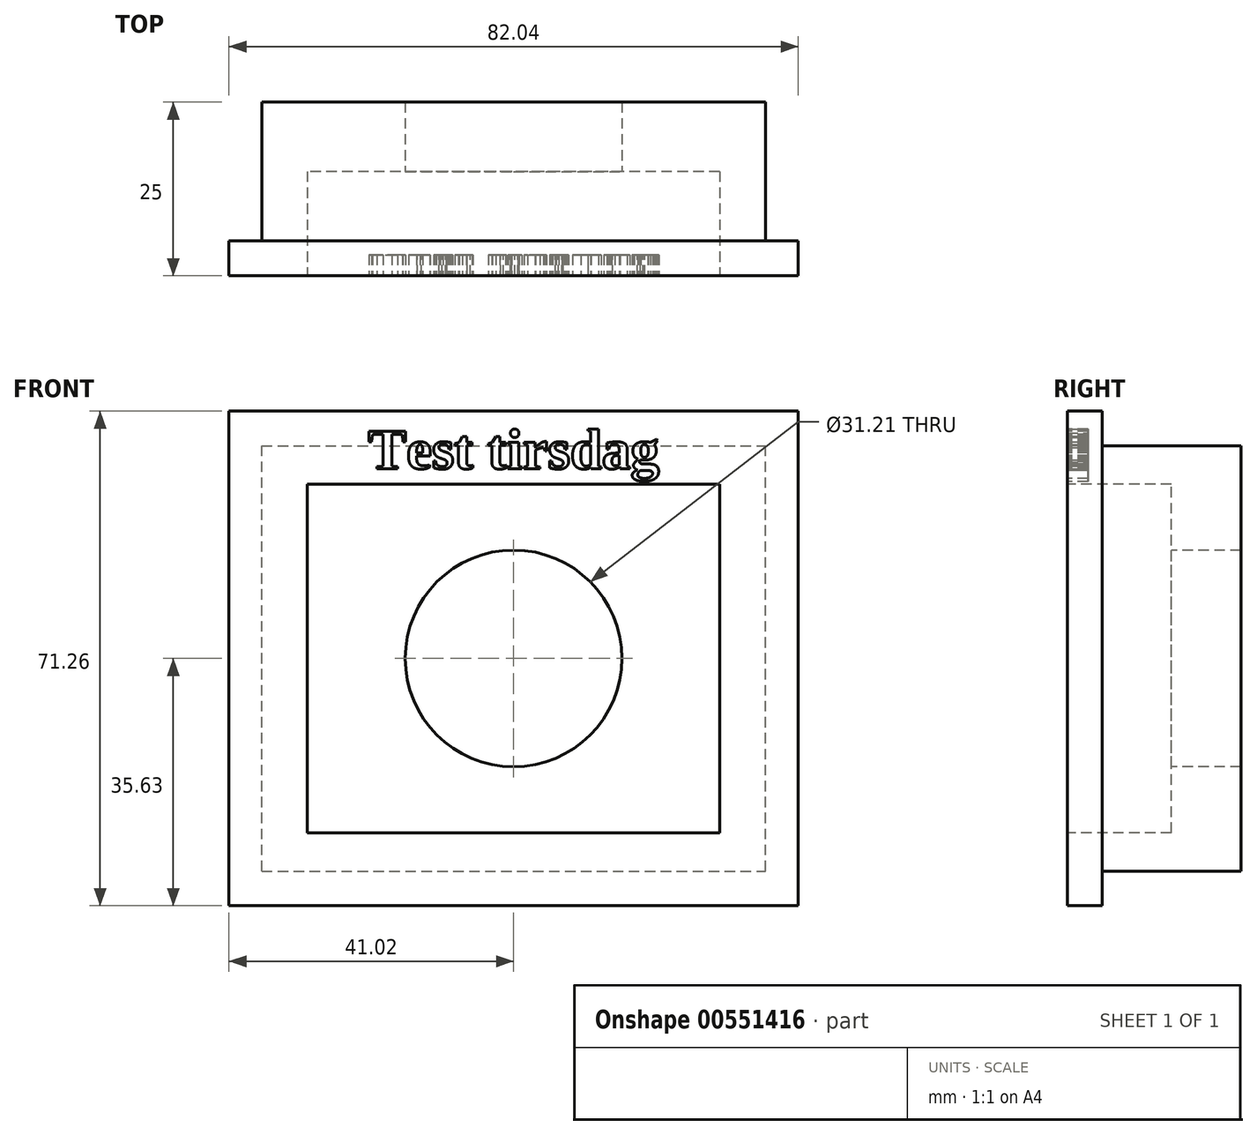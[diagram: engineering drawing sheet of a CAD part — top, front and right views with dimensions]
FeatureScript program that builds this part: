
annotation { "Feature Type Name" : "Feature", "Feature Type Description" : "" }
export const myFeature = defineFeature(function(context is Context, id is Id, definition is map)
    precondition{}
    {
        {
            var Q0;
            Q0=qCreatedBy(makeId("Front.planeOp"),FACE);
            var sketch = newSketch(context, id + "F0", { "sketchPlane" : qUnion([Q0])});
            skLineSegment(sketch, "E0.bottom", {"start": v(41.02, -35.63) * mm, "end": v(-41.02, -35.63) * mm});
            skLineSegment(sketch, "E0.top", {"start": v(41.02, 35.63) * mm, "end": v(-41.02, 35.63) * mm});
            skLineSegment(sketch, "E0.left", {"start": v(41.02, -35.63) * mm, "end": v(41.02, 35.63) * mm});
            skLineSegment(sketch, "E0.right", {"start": v(-41.02, -35.63) * mm, "end": v(-41.02, 35.63) * mm});
            skPoint(sketch, "E0.middle", {"position": v(0, 0) * mm});
            skSolve(sketch);
        }
        {
            var Q0;
            Q0=makeQuery(id+"F0.imprint","IMPRINT",FACE,{"disambiguationData":[TD([[makeQuery(id+"F0.imprint","IMPRINT",EDGE,{"derivedFrom":sQuery(id+"F0.wireOp",EDGE,"E0.bottom")}),-1.0]])]});
            extrude(context, id + "F1", {"entities" : qUnion([Q0]), "depth" : 25 * mm, "offsetDistance" : 25 * mm});
        }
        {
            var Q0;
            Q0=makeQuery(id+"F1.opExtrude","CAP_FACE",FACE,{"disambiguationData":[OSD([sQuery(id+"F0.wireOp",EDGE,"E0.bottom"),sQuery(id+"F0.wireOp",EDGE,"E0.top"),sQuery(id+"F0.wireOp",EDGE,"E0.left"),sQuery(id+"F0.wireOp",EDGE,"E0.right")])],"isStart":false});
            var sketch = newSketch(context, id + "F2", { "sketchPlane" : qUnion([Q0])});
            skLineSegment(sketch, "E1.bottom", {"start": v(29.71, -25.11) * mm, "end": v(-29.71, -25.11) * mm});
            skLineSegment(sketch, "E1.top", {"start": v(29.71, 25.11) * mm, "end": v(-29.71, 25.11) * mm});
            skLineSegment(sketch, "E1.left", {"start": v(29.71, -25.11) * mm, "end": v(29.71, 25.11) * mm});
            skLineSegment(sketch, "E1.right", {"start": v(-29.71, -25.11) * mm, "end": v(-29.71, 25.11) * mm});
            skPoint(sketch, "E1.middle", {"position": v(0, 0) * mm});
            skSolve(sketch);
        }
        {
            var Q0;
            Q0=makeQuery(id+"F2.imprint","IMPRINT",FACE,{"disambiguationData":[TD([[makeQuery(id+"F2.imprint","IMPRINT",EDGE,{"derivedFrom":sQuery(id+"F2.wireOp",EDGE,"E1.bottom")}),-1.0]])]});
            extrude(context, id + "F3", {"entities" : qUnion([Q0]), "operationType" : NewBodyOperationType.REMOVE, "oppositeDirection" : true, "depth" : 15 * mm, "offsetDistance" : 25 * mm});
        }
        {
            var Q0;
            Q0=makeQuery(id+"F1.opExtrude","CAP_FACE",FACE,{"disambiguationData":[OSD([sQuery(id+"F0.wireOp",EDGE,"E0.bottom"),sQuery(id+"F0.wireOp",EDGE,"E0.top"),sQuery(id+"F0.wireOp",EDGE,"E0.left"),sQuery(id+"F0.wireOp",EDGE,"E0.right")])],"isStart":true});
            var sketch = newSketch(context, id + "F4", { "sketchPlane" : qUnion([Q0])});
            skLineSegment(sketch, "E2.bottom", {"start": v(36.29, -30.63) * mm, "end": v(-36.29, -30.63) * mm});
            skLineSegment(sketch, "E2.top", {"start": v(36.29, 30.63) * mm, "end": v(-36.29, 30.63) * mm});
            skLineSegment(sketch, "E2.left", {"start": v(36.29, -30.63) * mm, "end": v(36.29, 30.63) * mm});
            skLineSegment(sketch, "E2.right", {"start": v(-36.29, -30.63) * mm, "end": v(-36.29, 30.63) * mm});
            skPoint(sketch, "E2.middle", {"position": v(0, 0) * mm});
            skSolve(sketch);
        }
        {
            var Q0;
            Q0=makeQuery(id+"F4.imprint","IMPRINT",FACE,{"disambiguationData":[TD([[makeQuery(id+"F4.imprint","IMPRINT",EDGE,{"derivedFrom":sQuery(id+"F4.wireOp",EDGE,"E2.bottom")}),1.0]])]});
            extrude(context, id + "F5", {"entities" : qUnion([Q0]), "operationType" : NewBodyOperationType.REMOVE, "oppositeDirection" : true, "depth" : 20 * mm, "offsetDistance" : 25 * mm});
        }
        {
            var Q0;
            Q0=makeQuery(id+"F3.boolean.opBoolean","COPY",FACE,{"derivedFrom":makeQuery(id+"F3.opExtrude","CAP_FACE",FACE,{"disambiguationData":[OSD([sQuery(id+"F2.wireOp",EDGE,"E1.bottom"),sQuery(id+"F2.wireOp",EDGE,"E1.top"),sQuery(id+"F2.wireOp",EDGE,"E1.left"),sQuery(id+"F2.wireOp",EDGE,"E1.right")])],"isStart":false})});
            var sketch = newSketch(context, id + "F6", { "sketchPlane" : qUnion([Q0])});
            skCircle(sketch, "E3", {"center": v(0, 0) * mm, "radius": 15.6 * mm});
            skSolve(sketch);
        }
        {
            var Q0;
            Q0=makeQuery(id+"F6.imprint","IMPRINT",FACE,{"disambiguationData":[TD([[makeQuery(id+"F6.imprint","IMPRINT",EDGE,{"derivedFrom":sQuery(id+"F6.wireOp",EDGE,"E3")}),1.0]])]});
            extrude(context, id + "F7", {"entities" : qUnion([Q0]), "operationType" : NewBodyOperationType.REMOVE, "oppositeDirection" : true, "depth" : 25 * mm, "offsetDistance" : 25 * mm});
        }
        {
            var Q0;
            Q0=makeQuery(id+"F1.opExtrude","CAP_FACE",FACE,{"disambiguationData":[OSD([sQuery(id+"F0.wireOp",EDGE,"E0.bottom"),sQuery(id+"F0.wireOp",EDGE,"E0.top"),sQuery(id+"F0.wireOp",EDGE,"E0.left"),sQuery(id+"F0.wireOp",EDGE,"E0.right")])],"isStart":false});
            var sketch = newSketch(context, id + "F8", { "sketchPlane" : qUnion([Q0])});
            skText(sketch, "E4", { "text": "Test tirsdag", "fontName": "Tinos-Bold.ttf"});
            const initialGuessF8  = {"E4": [-0.02094, 0.02733, 1, 0, 0.00594]};
            skSetInitialGuess(sketch, initialGuessF8);
            skSolve(sketch);
        }
        {
            var Q0;
            Q0 = qSketchRegion(id + "F8", true);
            extrude(context, id + "F9", {"entities" : qUnion([Q0]), "operationType" : NewBodyOperationType.REMOVE, "oppositeDirection" : true, "depth" : 3 * mm, "offsetDistance" : 25 * mm});
        }
    });
